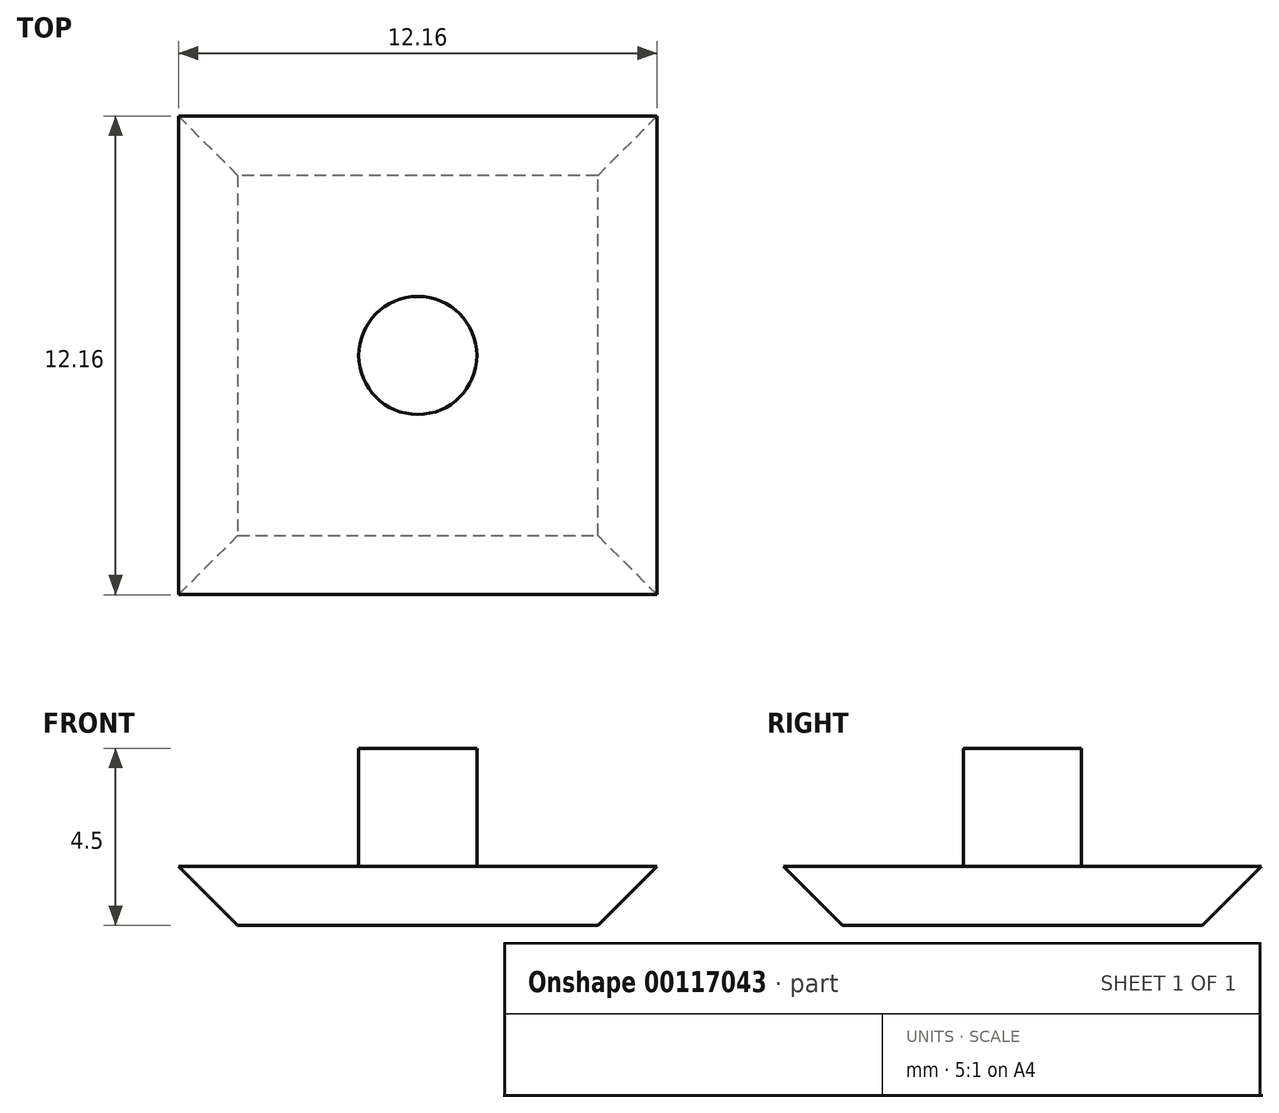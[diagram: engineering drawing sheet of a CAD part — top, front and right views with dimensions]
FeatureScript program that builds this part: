
annotation { "Feature Type Name" : "Feature", "Feature Type Description" : "" }
export const myFeature = defineFeature(function(context is Context, id is Id, definition is map)
    precondition{}
    {
        {
            var Q0;
            Q0=qCreatedBy(makeId("Top.planeOp"),FACE);
            var sketch = newSketch(context, id + "F0", { "sketchPlane" : qUnion([Q0])});
            skCircle(sketch, "E0", {"center": v(0, 0) * mm, "radius": 1.5 * mm});
            skSolve(sketch);
        }
        {
            var Q0;
            Q0 = qSketchRegion(id + "F0", true);
            extrude(context, id + "F1", {"entities" : qUnion([Q0]), "depth" : 3 * mm});
        }
        {
            var Q0;
            Q0=qCreatedBy(makeId("Top.planeOp"),FACE);
            var sketch = newSketch(context, id + "F2", { "sketchPlane" : qUnion([Q0])});
            skLineSegment(sketch, "E1.bottom", {"start": v(6.58, 6.58) * mm, "end": v(-6.58, 6.58) * mm});
            skLineSegment(sketch, "E1.top", {"start": v(6.58, -6.58) * mm, "end": v(-6.58, -6.58) * mm});
            skLineSegment(sketch, "E1.left", {"start": v(6.58, 6.58) * mm, "end": v(6.58, -6.58) * mm});
            skLineSegment(sketch, "E1.right", {"start": v(-6.58, 6.58) * mm, "end": v(-6.58, -6.58) * mm});
            skPoint(sketch, "E1.middle", {"position": v(0, 0) * mm});
            skSolve(sketch);
        }
        {
            var Q0;
            Q0=qCreatedBy(makeId("Right.planeOp"),FACE);
            var sketch = newSketch(context, id + "F3", { "sketchPlane" : qUnion([Q0])});
            skLineSegment(sketch, "E2.bottom", {"start": v(0, -6.08) * mm, "end": v(-22.45, 16.37) * mm});
            skLineSegment(sketch, "E2.top", {"start": v(22.45, 16.38) * mm, "end": v(0, 38.83) * mm});
            skLineSegment(sketch, "E2.left", {"start": v(0, -6.08) * mm, "end": v(22.45, 16.38) * mm});
            skLineSegment(sketch, "E2.right", {"start": v(-22.45, 16.37) * mm, "end": v(0, 38.83) * mm});
            skLineSegment(sketch, "E3", {"start": v(0, -6.08) * mm, "end": v(0, 38.83) * mm, "construction": true});
            skLineSegment(sketch, "E4", {"start": v(22.45, 16.38) * mm, "end": v(-22.45, 16.37) * mm, "construction": true});
            skLineSegment(sketch, "E5", {"start": v(6.08, 0) * mm, "end": v(-6.08, 0) * mm});
            skSolve(sketch);
        }
        {
            var Q0;
            Q0=qCreatedBy(makeId("Top.planeOp"),FACE);
            var sketch = newSketch(context, id + "F4", { "sketchPlane" : qUnion([Q0])});
            skLineSegment(sketch, "E6.bottom", {"start": v(-6.08, -6.08) * mm, "end": v(6.08, -6.08) * mm});
            skLineSegment(sketch, "E6.top", {"start": v(-6.08, 6.08) * mm, "end": v(6.08, 6.08) * mm});
            skLineSegment(sketch, "E6.left", {"start": v(-6.08, -6.08) * mm, "end": v(-6.08, 6.08) * mm});
            skLineSegment(sketch, "E6.right", {"start": v(6.08, -6.08) * mm, "end": v(6.08, 6.08) * mm});
            skPoint(sketch, "E6.middle", {"position": v(0, 0) * mm});
            skSolve(sketch);
        }
        {
            var Q0;
            Q0 = qSketchRegion(id + "F4", true);
            extrude(context, id + "F5", {"entities" : qUnion([Q0]), "operationType" : NewBodyOperationType.ADD, "oppositeDirection" : true, "depth" : 1.5 * mm, "hasDraft" : true, "draftAngle" : 45 * degree, "draftPullDirection" : true});
        }
    });
